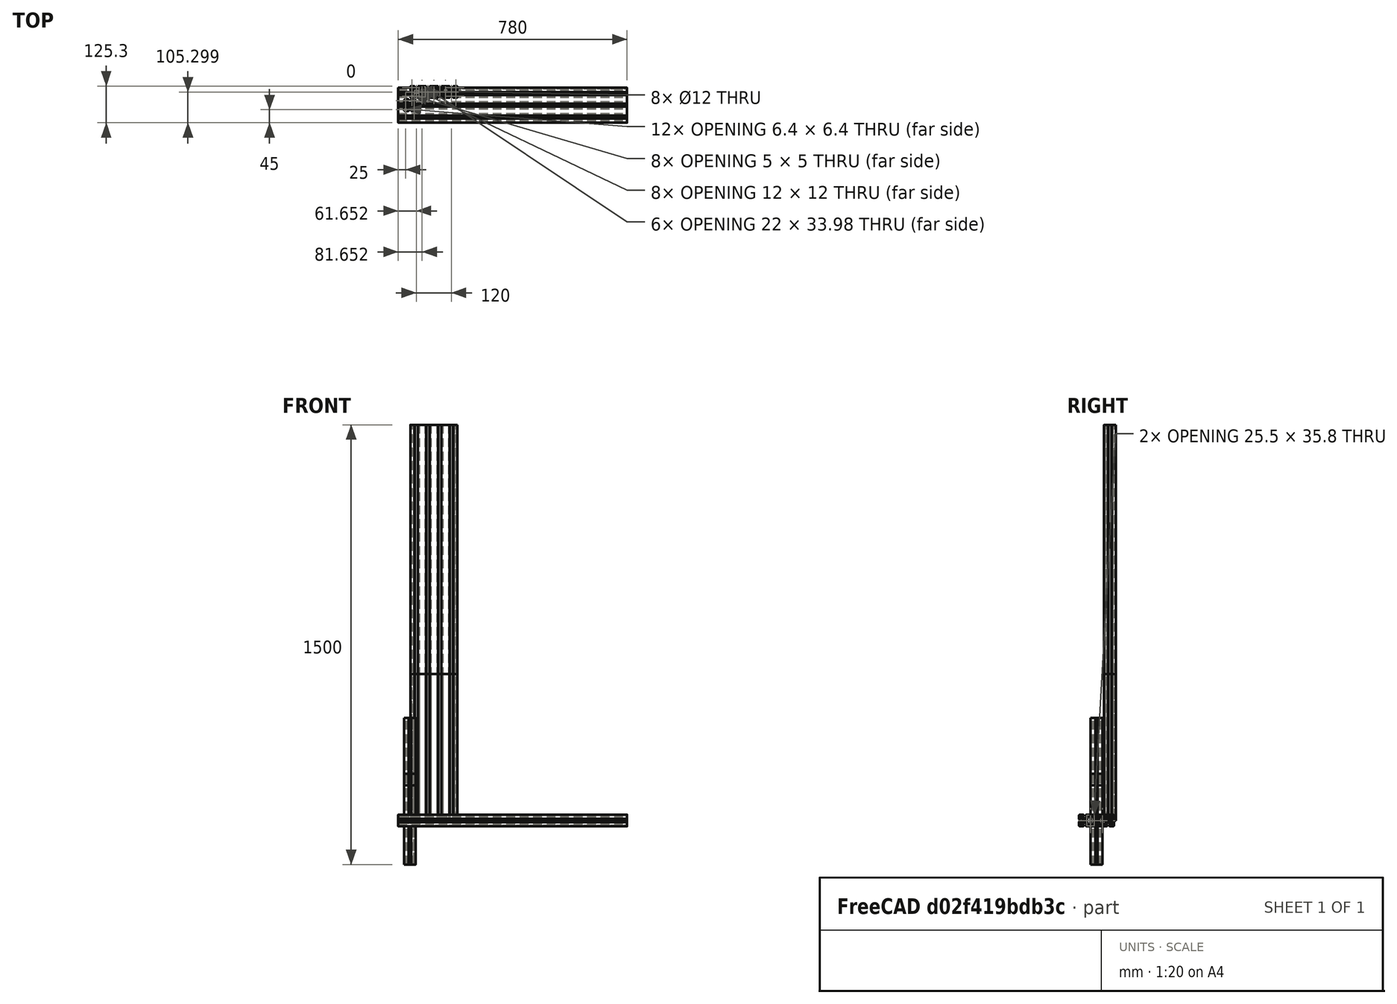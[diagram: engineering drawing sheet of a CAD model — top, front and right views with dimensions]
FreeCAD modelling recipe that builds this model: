
FCSTD DOCUMENT  (FreeCAD 1.0R39109 (Git))
Label: profile_40_serie
License: All rights reserved
LicenseURL: https://en.wikipedia.org/wiki/All_rights_reserved
objects: PartDesign::FeatureBase×6, PartDesign::Body×6, PartDesign::Pad×4, Part::Feature×3, PartDesign::Pocket×2
note: 39 computed .brp shape members not serialized (recipe doc carries the construction recipe); baked Part::Feature solids carry a one-line shape summary decoded from their .brp

FEATURE [Part::Feature] Part__Feature  label="profile_40x160x1000"
  shape: bbox 160 x 40 x 1000 mm, 262 faces (baked)
FEATURE [Part::Feature] Part__Feature003  label="profile_40x40x300"
  shape: bbox 40 x 40 x 300 mm, 147 faces (baked)
FEATURE [PartDesign::FeatureBase] BaseFeature
  BaseFeature = -> Part__Feature003
  Suppressed = false
FEATURE [PartDesign::Pad] Pad
  BaseFeature = -> BaseFeature
  Direction = (0,0,1)
  Length = 10
  Length2 = 10
  Profile = -> BaseFeature [Face147]
  Refine = true
  Suppressed = false
  Type = 0
FEATURE [PartDesign::Body] Body  label="profile_40x40x310"
  AllowCompound = false
  BaseFeature = -> Part__Feature003
  Group = -> [BaseFeature,Pad]
  Origin = -> Origin
  Tip = -> Pad
FEATURE [PartDesign::FeatureBase] BaseFeature001
  BaseFeature = -> Part__Feature
  Suppressed = false
FEATURE [PartDesign::Pad] Pad001
  BaseFeature = -> BaseFeature001
  Direction = (0,0,1)
  Length = 350
  Length2 = 10
  Profile = -> BaseFeature001 [Face9]
  Refine = true
  Suppressed = false
  Type = 0
FEATURE [PartDesign::Body] Body001  label="profile_40x160x1350"
  AllowCompound = false
  BaseFeature = -> Part__Feature
  Group = -> [BaseFeature001,Pad001]
  Origin = -> Origin001
  Tip = -> Pad001
FEATURE [PartDesign::FeatureBase] BaseFeature002
  BaseFeature = -> Part__Feature
  Suppressed = false
FEATURE [PartDesign::Pocket] Pocket
  BaseFeature = -> BaseFeature002
  Direction = (0,0,-1)
  Length = 500
  Length2 = 5
  Profile = -> BaseFeature002 [Face9]
  Refine = true
  Suppressed = false
  Type = 0
FEATURE [PartDesign::Body] Body002  label="profile_40x160x500"
  AllowCompound = false
  BaseFeature = -> Part__Feature
  Group = -> [BaseFeature002,Pocket]
  Origin = -> Origin002
  Tip = -> Pocket
FEATURE [PartDesign::FeatureBase] BaseFeature003
  BaseFeature = -> Part__Feature003
  Suppressed = false
FEATURE [PartDesign::Pad] Pad002
  BaseFeature = -> BaseFeature003
  Direction = (0,0,1)
  Length = 200
  Length2 = 10
  Profile = -> BaseFeature003 [Face147]
  Refine = true
  Suppressed = false
  Type = 0
FEATURE [PartDesign::Body] Body003  label="profile_40x40x500"
  AllowCompound = false
  BaseFeature = -> Part__Feature003
  Group = -> [BaseFeature003,Pad002]
  Origin = -> Origin003
  Tip = -> Pad002
FEATURE [Part::Feature] Part__Feature004  label="profile_40x120x80"
  shape: bbox 80 x 120 x 40 mm, 396 faces (baked)
FEATURE [PartDesign::FeatureBase] BaseFeature004
  BaseFeature = -> Part__Feature004
  Suppressed = false
FEATURE [PartDesign::Pad] Pad003
  BaseFeature = -> BaseFeature004
  Direction = (1,0,0)
  Length = 700
  Length2 = 10
  Profile = -> BaseFeature004 [Face396]
  Refine = true
  Suppressed = false
  Type = 0
FEATURE [PartDesign::Body] Body004  label="profile_40x120x780"
  AllowCompound = false
  BaseFeature = -> Part__Feature004
  Group = -> [BaseFeature004,Pad003]
  Origin = -> Origin004
  Tip = -> Pad003
FEATURE [PartDesign::FeatureBase] BaseFeature005
  BaseFeature = -> Part__Feature003
  Suppressed = false
FEATURE [PartDesign::Pocket] Pocket001
  BaseFeature = -> BaseFeature005
  Direction = (0,0,-1)
  Length = 30
  Length2 = 5
  Profile = -> BaseFeature005 [Face147]
  Refine = true
  Suppressed = false
  Type = 0
FEATURE [PartDesign::Body] Body005  label="profile_40x40x270"
  AllowCompound = false
  BaseFeature = -> Part__Feature003
  Group = -> [BaseFeature005,Pocket001]
  Origin = -> Origin005
  Tip = -> Pocket001
